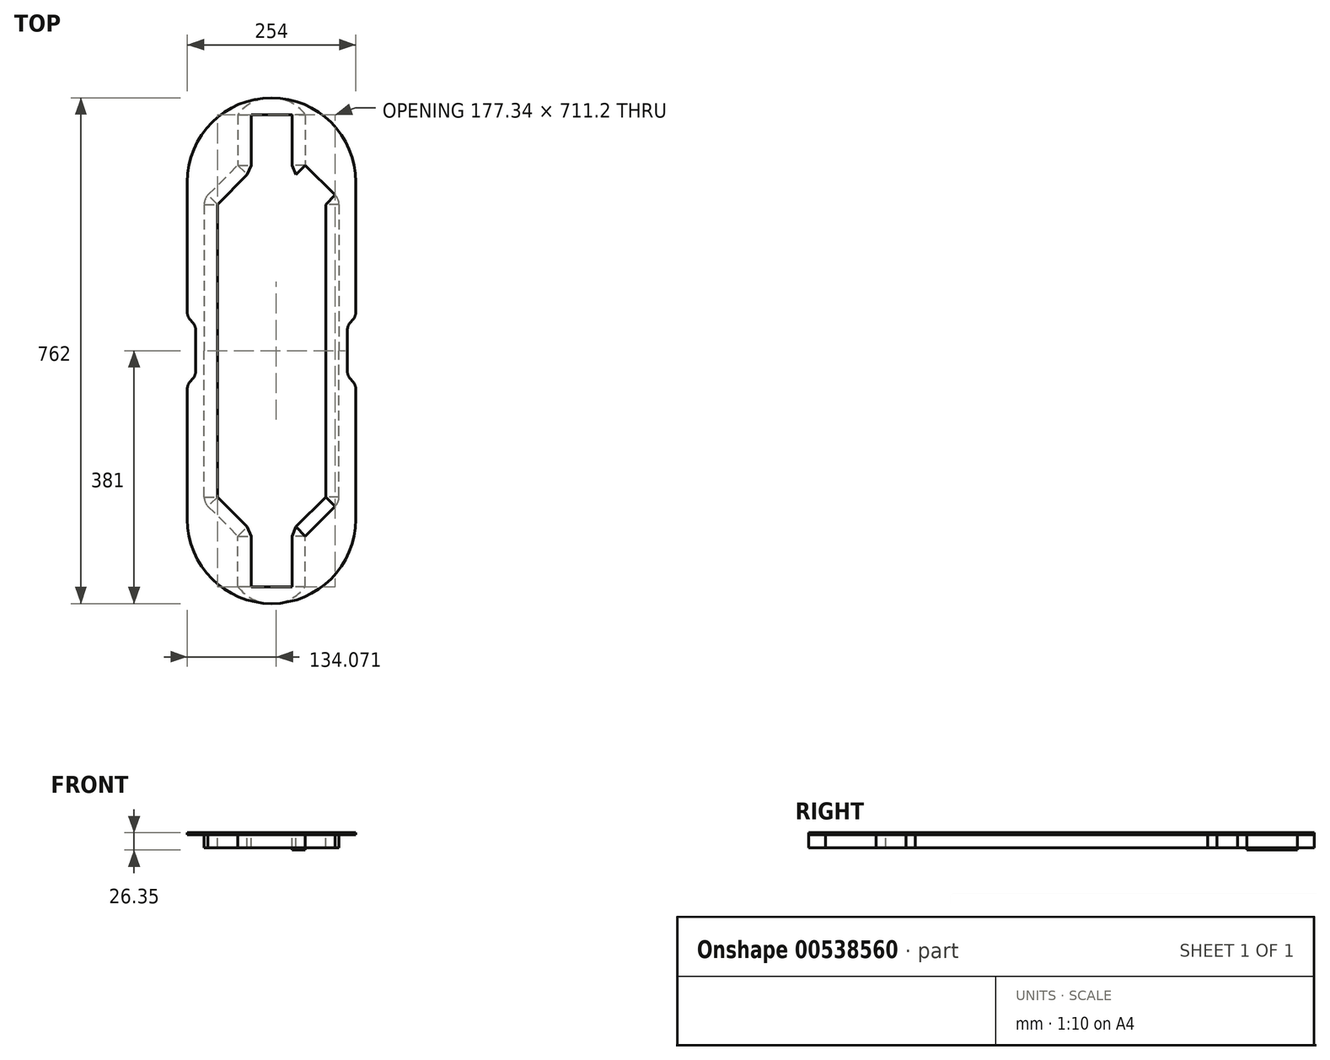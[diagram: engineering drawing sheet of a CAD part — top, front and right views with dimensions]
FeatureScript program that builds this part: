
annotation { "Feature Type Name" : "Feature", "Feature Type Description" : "" }
export const myFeature = defineFeature(function(context is Context, id is Id, definition is map)
    precondition{}
    {
        {
            var Q0;
            Q0=qCreatedBy(makeId("Top.planeOp"),FACE);
            var sketch = newSketch(context, id + "F0", { "sketchPlane" : qUnion([Q0])});
            skLineSegment(sketch, "E0.bottom", {"start": v(127, -381) * mm, "end": v(-127, -381) * mm, "construction": true});
            skLineSegment(sketch, "E0.top", {"start": v(127, 381) * mm, "end": v(-127, 381) * mm, "construction": true});
            skLineSegment(sketch, "E0.left", {"start": v(127, -381) * mm, "end": v(127, 381) * mm, "construction": true});
            skLineSegment(sketch, "E0.right", {"start": v(-127, -381) * mm, "end": v(-127, 381) * mm, "construction": true});
            skPoint(sketch, "E0.middle", {"position": v(0, 0) * mm});
            skLineSegment(sketch, "E1", {"start": v(0, 381) * mm, "end": v(0, -381) * mm, "construction": true});
            skLineSegment(sketch, "E2", {"start": v(-127, 0) * mm, "end": v(127, 0) * mm, "construction": true});
            skLineSegment(sketch, "E3.bottom", {"start": v(-50.8, 355.6) * mm, "end": v(-30.8, 355.6) * mm});
            skLineSegment(sketch, "E3.top", {"start": v(-50.8, 279.4) * mm, "end": v(-30.8, 279.4) * mm});
            skLineSegment(sketch, "E3.left", {"start": v(-50.8, 355.6) * mm, "end": v(-50.8, 279.4) * mm});
            skLineSegment(sketch, "E3.right", {"start": v(-30.8, 355.6) * mm, "end": v(-30.8, 279.4) * mm});
            skLineSegment(sketch, "E4.bottom", {"start": v(-101.6, 220.32) * mm, "end": v(-81.6, 220.32) * mm});
            skLineSegment(sketch, "E4.left", {"start": v(-101.6, 220.32) * mm, "end": v(-101.6, 0) * mm});
            skLineSegment(sketch, "E5", {"start": v(-81.6, 220.32) * mm, "end": v(-81.6, 0) * mm});
            skLineSegment(sketch, "E6.MirrorCS", {"start": v(50.8, 279.4) * mm, "end": v(30.8, 279.4) * mm});
            skLineSegment(sketch, "E7.MirrorCS", {"start": v(50.8, 355.6) * mm, "end": v(30.8, 355.6) * mm});
            skLineSegment(sketch, "E8.MirrorCS", {"start": v(30.8, 355.6) * mm, "end": v(30.8, 279.4) * mm});
            skLineSegment(sketch, "E9.MirrorCS", {"start": v(50.8, 355.6) * mm, "end": v(50.8, 279.4) * mm});
            skLineSegment(sketch, "E10.MirrorCS", {"start": v(101.6, 220.32) * mm, "end": v(81.6, 220.32) * mm});
            skLineSegment(sketch, "E11.MirrorCS", {"start": v(101.6, 220.32) * mm, "end": v(101.6, 0) * mm});
            skLineSegment(sketch, "E12.MirrorCS", {"start": v(81.6, 220.32) * mm, "end": v(81.6, 0) * mm});
            skArc(sketch, "E13", {"start": v(50.8, 355.6) * mm, "mid": v(0, 381) * mm, "end": v(-50.8, 355.6) * mm});
            skLineSegment(sketch, "E14.MirrorCS", {"start": v(-101.6, -220.32) * mm, "end": v(-81.6, -220.32) * mm});
            skLineSegment(sketch, "E15.MirrorCS", {"start": v(50.8, -355.6) * mm, "end": v(30.8, -355.6) * mm});
            skLineSegment(sketch, "E16.MirrorCS", {"start": v(50.8, -279.4) * mm, "end": v(30.8, -279.4) * mm});
            skLineSegment(sketch, "E17.MirrorCS", {"start": v(101.6, -220.32) * mm, "end": v(81.6, -220.32) * mm});
            skLineSegment(sketch, "E18.MirrorCS", {"start": v(-50.8, -279.4) * mm, "end": v(-30.8, -279.4) * mm});
            skLineSegment(sketch, "E19.MirrorCS", {"start": v(-50.8, -355.6) * mm, "end": v(-30.8, -355.6) * mm});
            skArc(sketch, "E20.MirrorCS", {"start": v(50.8, -355.6) * mm, "mid": v(0, -381) * mm, "end": v(-50.8, -355.6) * mm});
            skLineSegment(sketch, "E21.MirrorCS", {"start": v(-30.8, -355.6) * mm, "end": v(-30.8, -279.4) * mm});
            skLineSegment(sketch, "E22.MirrorCS", {"start": v(81.6, -220.32) * mm, "end": v(81.6, 0) * mm});
            skLineSegment(sketch, "E23.MirrorCS", {"start": v(50.8, -355.6) * mm, "end": v(50.8, -279.4) * mm});
            skLineSegment(sketch, "E24.MirrorCS", {"start": v(101.6, -220.32) * mm, "end": v(101.6, 0) * mm});
            skLineSegment(sketch, "E25.MirrorCS", {"start": v(-50.8, -355.6) * mm, "end": v(-50.8, -279.4) * mm});
            skLineSegment(sketch, "E26.MirrorCS", {"start": v(-81.6, -220.32) * mm, "end": v(-81.6, 0) * mm});
            skLineSegment(sketch, "E27.MirrorCS", {"start": v(-101.6, -220.32) * mm, "end": v(-101.6, 0) * mm});
            skLineSegment(sketch, "E28.MirrorCS", {"start": v(30.8, -355.6) * mm, "end": v(30.8, -279.4) * mm});
            skLineSegment(sketch, "E29", {"start": v(-50.8, 279.4) * mm, "end": v(-36.66, 265.26) * mm});
            skLineSegment(sketch, "E30", {"start": v(-36.66, 265.26) * mm, "end": v(-81.6, 220.32) * mm});
            skLineSegment(sketch, "E31", {"start": v(-81.6, 220.32) * mm, "end": v(-95.74, 234.46) * mm});
            skLineSegment(sketch, "E32", {"start": v(-95.74, 234.46) * mm, "end": v(-50.8, 279.4) * mm});
            skLineSegment(sketch, "E33.MirrorCS", {"start": v(50.8, 279.4) * mm, "end": v(36.66, 265.26) * mm});
            skLineSegment(sketch, "E34.MirrorCS", {"start": v(95.74, 234.46) * mm, "end": v(50.8, 279.4) * mm});
            skLineSegment(sketch, "E35.MirrorCS", {"start": v(81.6, 220.32) * mm, "end": v(95.74, 234.46) * mm});
            skLineSegment(sketch, "E36.MirrorCS", {"start": v(36.66, 265.26) * mm, "end": v(81.6, 220.32) * mm});
            skLineSegment(sketch, "E37.MirrorCS", {"start": v(50.8, -279.4) * mm, "end": v(36.66, -265.26) * mm});
            skLineSegment(sketch, "E38.MirrorCS", {"start": v(-50.8, -279.4) * mm, "end": v(-36.66, -265.26) * mm});
            skLineSegment(sketch, "E39.MirrorCS", {"start": v(-81.6, -220.32) * mm, "end": v(-95.74, -234.46) * mm});
            skLineSegment(sketch, "E40.MirrorCS", {"start": v(81.6, -220.32) * mm, "end": v(95.74, -234.46) * mm});
            skLineSegment(sketch, "E41.MirrorCS", {"start": v(95.74, -234.46) * mm, "end": v(50.8, -279.4) * mm});
            skLineSegment(sketch, "E42.MirrorCS", {"start": v(-36.66, -265.26) * mm, "end": v(-81.6, -220.32) * mm});
            skLineSegment(sketch, "E43.MirrorCS", {"start": v(36.66, -265.26) * mm, "end": v(81.6, -220.32) * mm});
            skLineSegment(sketch, "E44.MirrorCS", {"start": v(-95.74, -234.46) * mm, "end": v(-50.8, -279.4) * mm});
            skArc(sketch, "E45", {"start": v(-101.6, -220.32) * mm, "mid": v(-100.08, -227.97) * mm, "end": v(-95.74, -234.46) * mm});
            skArc(sketch, "E46.MirrorCS", {"start": v(-101.6, 220.32) * mm, "mid": v(-100.08, 227.97) * mm, "end": v(-95.74, 234.46) * mm});
            skLineSegment(sketch, "E47", {"start": v(-30.8, 355.6) * mm, "end": v(30.8, 355.6) * mm});
            skArc(sketch, "E48.MirrorCS", {"start": v(101.6, 220.32) * mm, "mid": v(100.08, 227.97) * mm, "end": v(95.74, 234.46) * mm});
            skArc(sketch, "E49.MirrorCS", {"start": v(101.6, -220.32) * mm, "mid": v(100.08, -227.97) * mm, "end": v(95.74, -234.46) * mm});
            skLineSegment(sketch, "E50.MirrorCS", {"start": v(-30.8, -355.6) * mm, "end": v(30.8, -355.6) * mm});
            skLineSegment(sketch, "E51", {"start": v(30.8, 279.4) * mm, "end": v(36.66, 265.26) * mm});
            skLineSegment(sketch, "E52", {"start": v(-30.8, 279.4) * mm, "end": v(-36.66, 265.26) * mm});
            skLineSegment(sketch, "E53", {"start": v(36.66, -265.26) * mm, "end": v(30.8, -279.4) * mm});
            skLineSegment(sketch, "E54", {"start": v(-30.8, -279.4) * mm, "end": v(-36.66, -265.26) * mm});
            skLineSegment(sketch, "E55", {"start": v(-114.3, 38.1) * mm, "end": v(-127, 50.8) * mm});
            skLineSegment(sketch, "E56", {"start": v(-127, 50.8) * mm, "end": v(-127, 254) * mm});
            skArc(sketch, "E57", {"start": v(0, 381) * mm, "mid": v(-89.8, 343.8) * mm, "end": v(-127, 254) * mm});
            skLineSegment(sketch, "E58.MirrorCS", {"start": v(114.3, 38.1) * mm, "end": v(127, 50.8) * mm});
            skLineSegment(sketch, "E59.MirrorCS", {"start": v(127, 50.8) * mm, "end": v(127, 254) * mm});
            skArc(sketch, "E60.MirrorCS", {"start": v(0, 381) * mm, "mid": v(89.8, 343.8) * mm, "end": v(127, 254) * mm});
            skLineSegment(sketch, "E61.MirrorCS", {"start": v(114.3, -38.1) * mm, "end": v(127, -50.8) * mm});
            skLineSegment(sketch, "E62.MirrorCS", {"start": v(127, -50.8) * mm, "end": v(127, -254) * mm});
            skArc(sketch, "E63.MirrorCS", {"start": v(0, -381) * mm, "mid": v(89.8, -343.8) * mm, "end": v(127, -254) * mm});
            skArc(sketch, "E64.MirrorCS", {"start": v(0, -381) * mm, "mid": v(-89.8, -343.8) * mm, "end": v(-127, -254) * mm});
            skLineSegment(sketch, "E65.MirrorCS", {"start": v(-127, -50.8) * mm, "end": v(-127, -254) * mm});
            skLineSegment(sketch, "E66.MirrorCS", {"start": v(-114.3, -38.1) * mm, "end": v(-127, -50.8) * mm});
            skLineSegment(sketch, "E67", {"start": v(-114.3, 38.1) * mm, "end": v(-114.3, 0) * mm});
            skLineSegment(sketch, "E68.MirrorCS", {"start": v(114.3, 38.1) * mm, "end": v(114.3, 0) * mm});
            skLineSegment(sketch, "E69.MirrorCS", {"start": v(-114.3, -38.1) * mm, "end": v(-114.3, 0) * mm});
            skLineSegment(sketch, "E70.MirrorCS", {"start": v(114.3, -38.1) * mm, "end": v(114.3, 0) * mm});
            skSolve(sketch);
        }
        {
            var Q0;
            Q0 = qSketchRegion(id + "F0", true);
            var Q1;
            Q1=makeQuery(id+"F0.imprint","IMPRINT",FACE,{"disambiguationData":[TD([[makeQuery(id+"F0.imprint","IMPRINT",EDGE,{"derivedFrom":sQuery(id+"F0.wireOp",EDGE,"E22.MirrorCS")}),1.0]])]});
            var Q2;
            Q2=makeQuery(id+"F0.imprint","IMPRINT",FACE,{"disambiguationData":[TD([[makeQuery(id+"F0.imprint","IMPRINT",EDGE,{"derivedFrom":sQuery(id+"F0.wireOp",EDGE,"E3.top")}),1.0]])]});
            var Q3;
            Q3=makeQuery(id+"F0.imprint","IMPRINT",FACE,{"disambiguationData":[TD([[makeQuery(id+"F0.imprint","IMPRINT",EDGE,{"derivedFrom":sQuery(id+"F0.wireOp",EDGE,"E3.top")}),-1.0]])]});
            var Q4;
            Q4=makeQuery(id+"F0.imprint","IMPRINT",FACE,{"disambiguationData":[TD([[makeQuery(id+"F0.imprint","IMPRINT",EDGE,{"derivedFrom":sQuery(id+"F0.wireOp",EDGE,"E31")}),-1.0]])]});
            var Q5;
            Q5=makeQuery(id+"F0.imprint","IMPRINT",FACE,{"disambiguationData":[TD([[makeQuery(id+"F0.imprint","IMPRINT",EDGE,{"derivedFrom":sQuery(id+"F0.wireOp",EDGE,"E4.bottom")}),1.0]])]});
            var Q6;
            Q6=makeQuery(id+"F0.imprint","IMPRINT",FACE,{"disambiguationData":[TD([[makeQuery(id+"F0.imprint","IMPRINT",EDGE,{"derivedFrom":sQuery(id+"F0.wireOp",EDGE,"E6.MirrorCS")}),-1.0]])]});
            var Q7;
            Q7=makeQuery(id+"F0.imprint","IMPRINT",FACE,{"disambiguationData":[TD([[makeQuery(id+"F0.imprint","IMPRINT",EDGE,{"derivedFrom":sQuery(id+"F0.wireOp",EDGE,"E6.MirrorCS")}),1.0]])]});
            var Q8;
            Q8=makeQuery(id+"F0.imprint","IMPRINT",FACE,{"disambiguationData":[TD([[makeQuery(id+"F0.imprint","IMPRINT",EDGE,{"derivedFrom":sQuery(id+"F0.wireOp",EDGE,"E35.MirrorCS")}),1.0]])]});
            var Q9;
            Q9=makeQuery(id+"F0.imprint","IMPRINT",FACE,{"disambiguationData":[TD([[makeQuery(id+"F0.imprint","IMPRINT",EDGE,{"derivedFrom":sQuery(id+"F0.wireOp",EDGE,"E10.MirrorCS")}),-1.0]])]});
            var Q10;
            Q10=makeQuery(id+"F0.imprint","IMPRINT",FACE,{"disambiguationData":[TD([[makeQuery(id+"F0.imprint","IMPRINT",EDGE,{"derivedFrom":sQuery(id+"F0.wireOp",EDGE,"E14.MirrorCS")}),-1.0]])]});
            var Q11;
            Q11=makeQuery(id+"F0.imprint","IMPRINT",FACE,{"disambiguationData":[TD([[makeQuery(id+"F0.imprint","IMPRINT",EDGE,{"derivedFrom":sQuery(id+"F0.wireOp",EDGE,"E39.MirrorCS")}),1.0]])]});
            var Q12;
            Q12=makeQuery(id+"F0.imprint","IMPRINT",FACE,{"disambiguationData":[TD([[makeQuery(id+"F0.imprint","IMPRINT",EDGE,{"derivedFrom":sQuery(id+"F0.wireOp",EDGE,"E18.MirrorCS")}),1.0]])]});
            var Q13;
            Q13=makeQuery(id+"F0.imprint","IMPRINT",FACE,{"disambiguationData":[TD([[makeQuery(id+"F0.imprint","IMPRINT",EDGE,{"derivedFrom":sQuery(id+"F0.wireOp",EDGE,"E18.MirrorCS")}),-1.0]])]});
            var Q14;
            Q14=makeQuery(id+"F0.imprint","IMPRINT",FACE,{"disambiguationData":[TD([[makeQuery(id+"F0.imprint","IMPRINT",EDGE,{"derivedFrom":sQuery(id+"F0.wireOp",EDGE,"E16.MirrorCS")}),1.0]])]});
            var Q15;
            Q15=makeQuery(id+"F0.imprint","IMPRINT",FACE,{"disambiguationData":[TD([[makeQuery(id+"F0.imprint","IMPRINT",EDGE,{"derivedFrom":sQuery(id+"F0.wireOp",EDGE,"E16.MirrorCS")}),-1.0]])]});
            var Q16;
            Q16=makeQuery(id+"F0.imprint","IMPRINT",FACE,{"disambiguationData":[TD([[makeQuery(id+"F0.imprint","IMPRINT",EDGE,{"derivedFrom":sQuery(id+"F0.wireOp",EDGE,"E40.MirrorCS")}),-1.0]])]});
            var Q17;
            Q17=makeQuery(id+"F0.imprint","IMPRINT",FACE,{"disambiguationData":[TD([[makeQuery(id+"F0.imprint","IMPRINT",EDGE,{"derivedFrom":sQuery(id+"F0.wireOp",EDGE,"E17.MirrorCS")}),1.0]])]});
            var Q18;
            Q18=makeQuery(id+"F0.imprint","IMPRINT",FACE,{"disambiguationData":[TD([[makeQuery(id+"F0.imprint","IMPRINT",EDGE,{"derivedFrom":sQuery(id+"F0.wireOp",EDGE,"E26.MirrorCS")}),1.0]])]});
            var Q19;
            Q19=makeQuery(id+"F0.imprint","IMPRINT",FACE,{"disambiguationData":[TD([[makeQuery(id+"F0.imprint","IMPRINT",EDGE,{"derivedFrom":sQuery(id+"F0.wireOp",EDGE,"E22.MirrorCS")}),-1.0]])]});
            extrude(context, id + "F1", {"entities" : qUnion([Q0, Q1, Q2, Q3, Q4, Q5, Q6, Q7, Q8, Q9, Q10, Q11, Q12, Q13, Q14, Q15, Q16, Q17, Q18, Q19]), "depth" : 3.17 * mm, "offsetDistance" : 25.4 * mm});
        }
        {
            var Q0;
            Q0=makeQuery(id+"F0.imprint","IMPRINT",FACE,{"disambiguationData":[TD([[makeQuery(id+"F0.imprint","IMPRINT",EDGE,{"derivedFrom":sQuery(id+"F0.wireOp",EDGE,"E3.top")}),1.0]])]});
            var Q1;
            Q1=makeQuery(id+"F0.imprint","IMPRINT",FACE,{"disambiguationData":[TD([[makeQuery(id+"F0.imprint","IMPRINT",EDGE,{"derivedFrom":sQuery(id+"F0.wireOp",EDGE,"E6.MirrorCS")}),-1.0]])]});
            var Q2;
            Q2=makeQuery(id+"F0.imprint","IMPRINT",FACE,{"disambiguationData":[TD([[makeQuery(id+"F0.imprint","IMPRINT",EDGE,{"derivedFrom":sQuery(id+"F0.wireOp",EDGE,"E35.MirrorCS")}),1.0]])]});
            var Q3;
            Q3=makeQuery(id+"F0.imprint","IMPRINT",FACE,{"disambiguationData":[TD([[makeQuery(id+"F0.imprint","IMPRINT",EDGE,{"derivedFrom":sQuery(id+"F0.wireOp",EDGE,"E31")}),-1.0]])]});
            var Q4;
            Q4=makeQuery(id+"F0.imprint","IMPRINT",FACE,{"disambiguationData":[TD([[makeQuery(id+"F0.imprint","IMPRINT",EDGE,{"derivedFrom":sQuery(id+"F0.wireOp",EDGE,"E26.MirrorCS")}),1.0]])]});
            var Q5;
            Q5=makeQuery(id+"F0.imprint","IMPRINT",FACE,{"disambiguationData":[TD([[makeQuery(id+"F0.imprint","IMPRINT",EDGE,{"derivedFrom":sQuery(id+"F0.wireOp",EDGE,"E22.MirrorCS")}),-1.0]])]});
            var Q6;
            Q6=makeQuery(id+"F0.imprint","IMPRINT",FACE,{"disambiguationData":[TD([[makeQuery(id+"F0.imprint","IMPRINT",EDGE,{"derivedFrom":sQuery(id+"F0.wireOp",EDGE,"E38.MirrorCS")}),1.0]])]});
            var Q7;
            Q7=makeQuery(id+"F0.imprint","IMPRINT",FACE,{"disambiguationData":[TD([[makeQuery(id+"F0.imprint","IMPRINT",EDGE,{"derivedFrom":sQuery(id+"F0.wireOp",EDGE,"E37.MirrorCS")}),-1.0]])]});
            var Q8;
            Q8=makeQuery(id+"F0.imprint","IMPRINT",FACE,{"disambiguationData":[TD([[makeQuery(id+"F0.imprint","IMPRINT",EDGE,{"derivedFrom":sQuery(id+"F0.wireOp",EDGE,"E15.MirrorCS")}),-1.0]])]});
            var Q9;
            Q9=makeQuery(id+"F0.imprint","IMPRINT",FACE,{"disambiguationData":[TD([[makeQuery(id+"F0.imprint","IMPRINT",EDGE,{"derivedFrom":sQuery(id+"F0.wireOp",EDGE,"E19.MirrorCS")}),1.0]])]});
            var Q10;
            Q10=makeQuery(id+"F0.imprint","IMPRINT",FACE,{"disambiguationData":[TD([[makeQuery(id+"F0.imprint","IMPRINT",EDGE,{"derivedFrom":sQuery(id+"F0.wireOp",EDGE,"E39.MirrorCS")}),1.0]])]});
            var Q11;
            Q11=makeQuery(id+"F0.imprint","IMPRINT",FACE,{"disambiguationData":[TD([[makeQuery(id+"F0.imprint","IMPRINT",EDGE,{"derivedFrom":sQuery(id+"F0.wireOp",EDGE,"E18.MirrorCS")}),-1.0]])]});
            var Q12;
            Q12=makeQuery(id+"F0.imprint","IMPRINT",FACE,{"disambiguationData":[TD([[makeQuery(id+"F0.imprint","IMPRINT",EDGE,{"derivedFrom":sQuery(id+"F0.wireOp",EDGE,"E16.MirrorCS")}),1.0]])]});
            var Q13;
            Q13=makeQuery(id+"F0.imprint","IMPRINT",FACE,{"disambiguationData":[TD([[makeQuery(id+"F0.imprint","IMPRINT",EDGE,{"derivedFrom":sQuery(id+"F0.wireOp",EDGE,"E40.MirrorCS")}),-1.0]])]});
            extrude(context, id + "F2", {"entities" : qUnion([Q0, Q1, Q2, Q3, Q4, Q5, Q6, Q7, Q8, Q9, Q10, Q11, Q12, Q13]), "oppositeDirection" : true, "depth" : 20 * mm, "offsetDistance" : 25.4 * mm});
        }
        {
            var Q0;
            Q0=makeQuery(id+"F0.imprint","IMPRINT",FACE,{"disambiguationData":[TD([[makeQuery(id+"F0.imprint","IMPRINT",EDGE,{"derivedFrom":sQuery(id+"F0.wireOp",EDGE,"E13")}),1.0]])]});
            var Q1;
            Q1=makeQuery(id+"F0.imprint","IMPRINT",FACE,{"disambiguationData":[TD([[makeQuery(id+"F0.imprint","IMPRINT",EDGE,{"derivedFrom":sQuery(id+"F0.wireOp",EDGE,"E6.MirrorCS")}),1.0]])]});
            var Q2;
            Q2=makeQuery(id+"F0.imprint","IMPRINT",FACE,{"disambiguationData":[TD([[makeQuery(id+"F0.imprint","IMPRINT",EDGE,{"derivedFrom":sQuery(id+"F0.wireOp",EDGE,"E10.MirrorCS")}),-1.0]])]});
            var Q3;
            Q3=makeQuery(id+"F0.imprint","IMPRINT",FACE,{"disambiguationData":[TD([[makeQuery(id+"F0.imprint","IMPRINT",EDGE,{"derivedFrom":sQuery(id+"F0.wireOp",EDGE,"E4.bottom")}),1.0]])]});
            var Q4;
            Q4=makeQuery(id+"F0.imprint","IMPRINT",FACE,{"disambiguationData":[TD([[makeQuery(id+"F0.imprint","IMPRINT",EDGE,{"derivedFrom":sQuery(id+"F0.wireOp",EDGE,"E3.top")}),-1.0]])]});
            var Q5;
            Q5=makeQuery(id+"F0.imprint","IMPRINT",FACE,{"disambiguationData":[TD([[makeQuery(id+"F0.imprint","IMPRINT",EDGE,{"derivedFrom":sQuery(id+"F0.wireOp",EDGE,"E17.MirrorCS")}),1.0]])]});
            var Q6;
            Q6=makeQuery(id+"F0.imprint","IMPRINT",FACE,{"disambiguationData":[TD([[makeQuery(id+"F0.imprint","IMPRINT",EDGE,{"derivedFrom":sQuery(id+"F0.wireOp",EDGE,"E19.MirrorCS")}),-1.0]])]});
            var Q7;
            Q7=makeQuery(id+"F0.imprint","IMPRINT",FACE,{"disambiguationData":[TD([[makeQuery(id+"F0.imprint","IMPRINT",EDGE,{"derivedFrom":sQuery(id+"F0.wireOp",EDGE,"E16.MirrorCS")}),-1.0]])]});
            var Q8;
            Q8=makeQuery(id+"F0.imprint","IMPRINT",FACE,{"disambiguationData":[TD([[makeQuery(id+"F0.imprint","IMPRINT",EDGE,{"derivedFrom":sQuery(id+"F0.wireOp",EDGE,"E18.MirrorCS")}),1.0]])]});
            var Q9;
            Q9=makeQuery(id+"F0.imprint","IMPRINT",FACE,{"disambiguationData":[TD([[makeQuery(id+"F0.imprint","IMPRINT",EDGE,{"derivedFrom":sQuery(id+"F0.wireOp",EDGE,"E14.MirrorCS")}),-1.0]])]});
            extrude(context, id + "F3", {"entities" : qUnion([Q0, Q1, Q2, Q3, Q4, Q5, Q6, Q7, Q8, Q9]), "oppositeDirection" : true, "depth" : 20 * mm, "offsetDistance" : 25.4 * mm});
        }
        {
            var Q0;
            Q0=makeQuery(id+"F1.opExtrude","SWEPT_EDGE",EDGE,{"disambiguationData":[OSD([sQuery(id+"F0.wireOp",EDGE,"E61.MirrorCS"),sQuery(id+"F0.wireOp",EDGE,"E62.MirrorCS")])]});
            var Q1;
            Q1=makeQuery(id+"F1.opExtrude","SWEPT_EDGE",EDGE,{"disambiguationData":[OSD([sQuery(id+"F0.wireOp",EDGE,"E24.MirrorCS"),sQuery(id+"F0.wireOp",EDGE,"E61.MirrorCS")])]});
            var Q2;
            Q2=makeQuery(id+"F1.opExtrude","SWEPT_EDGE",EDGE,{"disambiguationData":[OSD([sQuery(id+"F0.wireOp",EDGE,"E11.MirrorCS"),sQuery(id+"F0.wireOp",EDGE,"E58.MirrorCS")])]});
            var Q3;
            Q3=makeQuery(id+"F1.opExtrude","SWEPT_EDGE",EDGE,{"disambiguationData":[OSD([sQuery(id+"F0.wireOp",EDGE,"E58.MirrorCS"),sQuery(id+"F0.wireOp",EDGE,"E59.MirrorCS")])]});
            var Q4;
            Q4=makeQuery(id+"F1.opExtrude","SWEPT_EDGE",EDGE,{"disambiguationData":[OSD([sQuery(id+"F0.wireOp",EDGE,"E65.MirrorCS"),sQuery(id+"F0.wireOp",EDGE,"E66.MirrorCS")])]});
            var Q5;
            Q5=makeQuery(id+"F1.opExtrude","SWEPT_EDGE",EDGE,{"disambiguationData":[OSD([sQuery(id+"F0.wireOp",EDGE,"E27.MirrorCS"),sQuery(id+"F0.wireOp",EDGE,"E66.MirrorCS")])]});
            var Q6;
            Q6=makeQuery(id+"F1.opExtrude","SWEPT_EDGE",EDGE,{"disambiguationData":[OSD([sQuery(id+"F0.wireOp",EDGE,"E4.left"),sQuery(id+"F0.wireOp",EDGE,"E55")])]});
            var Q7;
            Q7=makeQuery(id+"F1.opExtrude","SWEPT_EDGE",EDGE,{"disambiguationData":[OSD([sQuery(id+"F0.wireOp",EDGE,"E55"),sQuery(id+"F0.wireOp",EDGE,"E56")])]});
            fillet(context, id + "F4", {"entities" : qUnion([Q0, Q1, Q2, Q3, Q4, Q5, Q6, Q7]), "radius" : 19.05 * mm, "tangentPropagation" : true, "allowEdgeOverflow" : false});
        }
        {
            var Q0;
            Q0=makeQuery(id+"F2.opExtrude","CAP_FACE",FACE,{"disambiguationData":[OSD([sQuery(id+"F0.wireOp",EDGE,"E6.MirrorCS"),sQuery(id+"F0.wireOp",EDGE,"E7.MirrorCS"),sQuery(id+"F0.wireOp",EDGE,"E8.MirrorCS"),sQuery(id+"F0.wireOp",EDGE,"E9.MirrorCS")])],"isStart":false});
            var sketch = newSketch(context, id + "F5", { "sketchPlane" : qUnion([Q0])});
            skArc(sketch, "E71.0", {"start": v(50.8, -355.6) * mm, "mid": v(0, -381) * mm, "end": v(-50.8, -355.6) * mm});
            skArc(sketch, "E71.1", {"start": v(50.8, 355.6) * mm, "mid": v(0, 381) * mm, "end": v(-50.8, 355.6) * mm});
            skLineSegment(sketch, "E71.2", {"start": v(50.8, 355.6) * mm, "end": v(50.8, 279.4) * mm});
            skLineSegment(sketch, "E71.3", {"start": v(95.74, 234.46) * mm, "end": v(50.8, 279.4) * mm});
            skArc(sketch, "E71.4", {"start": v(101.6, 220.32) * mm, "mid": v(100.08, 227.97) * mm, "end": v(95.74, 234.46) * mm});
            skLineSegment(sketch, "E71.5", {"start": v(101.6, -220.32) * mm, "end": v(101.6, 220.32) * mm});
            skLineSegment(sketch, "E71.6", {"start": v(-50.8, 355.6) * mm, "end": v(-50.8, 279.4) * mm});
            skLineSegment(sketch, "E71.7", {"start": v(-95.74, 234.46) * mm, "end": v(-50.8, 279.4) * mm});
            skArc(sketch, "E71.8", {"start": v(-101.6, 220.32) * mm, "mid": v(-100.08, 227.97) * mm, "end": v(-95.74, 234.46) * mm});
            skLineSegment(sketch, "E71.9", {"start": v(-101.6, -220.32) * mm, "end": v(-101.6, 220.32) * mm});
            skArc(sketch, "E71.10", {"start": v(-101.6, -220.32) * mm, "mid": v(-100.08, -227.97) * mm, "end": v(-95.74, -234.46) * mm});
            skLineSegment(sketch, "E71.11", {"start": v(-95.74, -234.46) * mm, "end": v(-50.8, -279.4) * mm});
            skLineSegment(sketch, "E71.12", {"start": v(-50.8, -355.6) * mm, "end": v(-50.8, -279.4) * mm});
            skLineSegment(sketch, "E71.13", {"start": v(50.8, -355.6) * mm, "end": v(50.8, -279.4) * mm});
            skLineSegment(sketch, "E71.14", {"start": v(95.74, -234.46) * mm, "end": v(50.8, -279.4) * mm});
            skArc(sketch, "E71.15", {"start": v(101.6, -220.32) * mm, "mid": v(100.08, -227.97) * mm, "end": v(95.74, -234.46) * mm});
            skSolve(sketch);
        }
        {
            var Q0;
            Q0=makeQuery(id+"F5.imprint","IMPRINT",FACE,{"disambiguationData":[TD([[makeQuery(id+"F5.imprint","IMPRINT",EDGE,{"derivedFrom":sQuery(id+"F5.wireOp",EDGE,"E71.0")}),-1.0]])]});
            var Q1;
            Q1=makeQuery(id+"F5.imprint","IMPRINT",FACE,{"disambiguationData":[TD([[makeQuery(id+"F5.imprint","IMPRINT",EDGE,{"derivedFrom":sQuery(id+"F5.wireOp",EDGE,"E71.13")}),1.0]])]});
            extrude(context, id + "F6", {"entities" : qUnion([Q0, Q1]), "depth" : 3.17 * mm, "offsetDistance" : 25.4 * mm});
        }
    });
